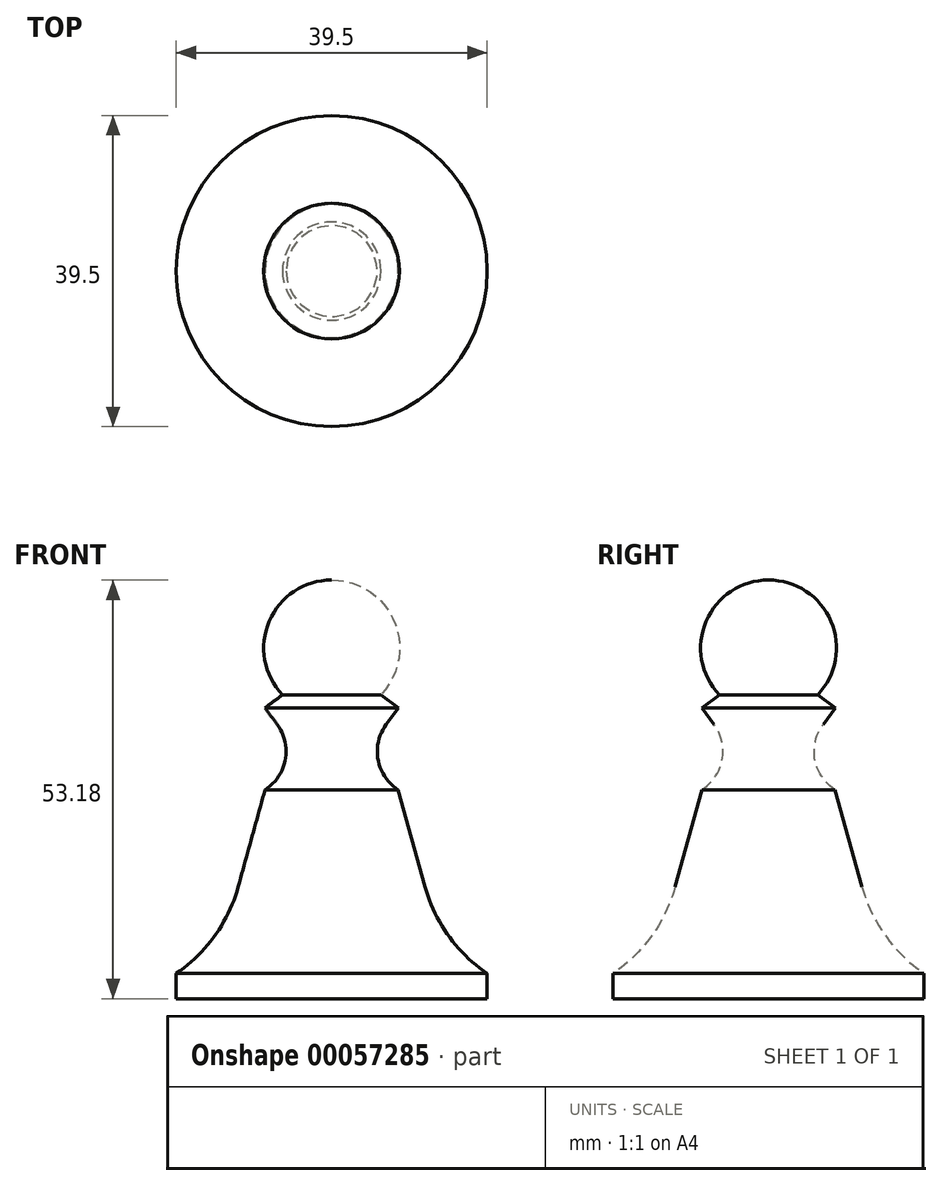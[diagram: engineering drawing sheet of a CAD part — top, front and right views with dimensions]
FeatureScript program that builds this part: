
annotation { "Feature Type Name" : "Feature", "Feature Type Description" : "" }
export const myFeature = defineFeature(function(context is Context, id is Id, definition is map)
    precondition{}
    {
        {
            var Q0;
            Q0=qCreatedBy(makeId("Front.planeOp"),FACE);
            var sketch = newSketch(context, id + "F0", { "sketchPlane" : qUnion([Q0])});
            skLineSegment(sketch, "E0", {"start": v(0, 0) * mm, "end": v(19.75, 0) * mm});
            skLineSegment(sketch, "E1", {"start": v(19.75, 0) * mm, "end": v(19.75, 3.2) * mm});
            skLineSegment(sketch, "E2", {"start": v(0, 0) * mm, "end": v(0, 38.6) * mm});
            skLineSegment(sketch, "E3", {"start": v(19.75, 3.2) * mm, "end": v(14.2, 5.81) * mm});
            skLineSegment(sketch, "E4", {"start": v(14.2, 5.81) * mm, "end": v(8.46, 26.55) * mm});
            skArc(sketch, "E5", {"start": v(6.94, 34.86) * mm, "mid": v(5.9, 30.38) * mm, "end": v(8.46, 26.55) * mm});
            skLineSegment(sketch, "E6", {"start": v(6.94, 34.86) * mm, "end": v(8.48, 36.93) * mm});
            skLineSegment(sketch, "E7", {"start": v(8.48, 36.93) * mm, "end": v(6.25, 38.6) * mm});
            skArc(sketch, "E8", {"start": v(6.25, 38.6) * mm, "mid": v(7.94, 47.95) * mm, "end": v(0, 53.18) * mm});
            skLineSegment(sketch, "E9", {"start": v(0, 53.18) * mm, "end": v(16.2, 53.18) * mm, "construction": true});
            skLineSegment(sketch, "E10", {"start": v(6.25, 38.6) * mm, "end": v(0, 38.6) * mm, "construction": true});
            skLineSegment(sketch, "E11", {"start": v(0, 38.6) * mm, "end": v(0, 53.18) * mm});
            skSolve(sketch);
        }
        {
            var Q0;
            Q0=makeQuery(id+"F0.imprint","IMPRINT",FACE,{"disambiguationData":[TD([[makeQuery(id+"F0.imprint","IMPRINT",EDGE,{"derivedFrom":sQuery(id+"F0.wireOp",EDGE,"E0")}),1.0]])]});
            var Q1;
            Q1=sQuery(id+"F0.wireOp",EDGE,"E2");
            revolve(context, id + "F1", {"entities" : qUnion([Q0]), "axis" : qUnion([Q1]), "revolveType" : RevolveType.FULL});
        }
        {
            var Q0;
            Q0=makeQuery(id+"F1.opRevolve","SWEPT_EDGE",EDGE,{"disambiguationData":[OSD([sQuery(id+"F0.wireOp",EDGE,"E3"),sQuery(id+"F0.wireOp",EDGE,"E4")])]});
            fillet(context, id + "F2", {"entities" : qUnion([Q0]), "radius" : 19.73 * mm, "tangentPropagation" : true, "allowEdgeOverflow" : false});
        }
    });
